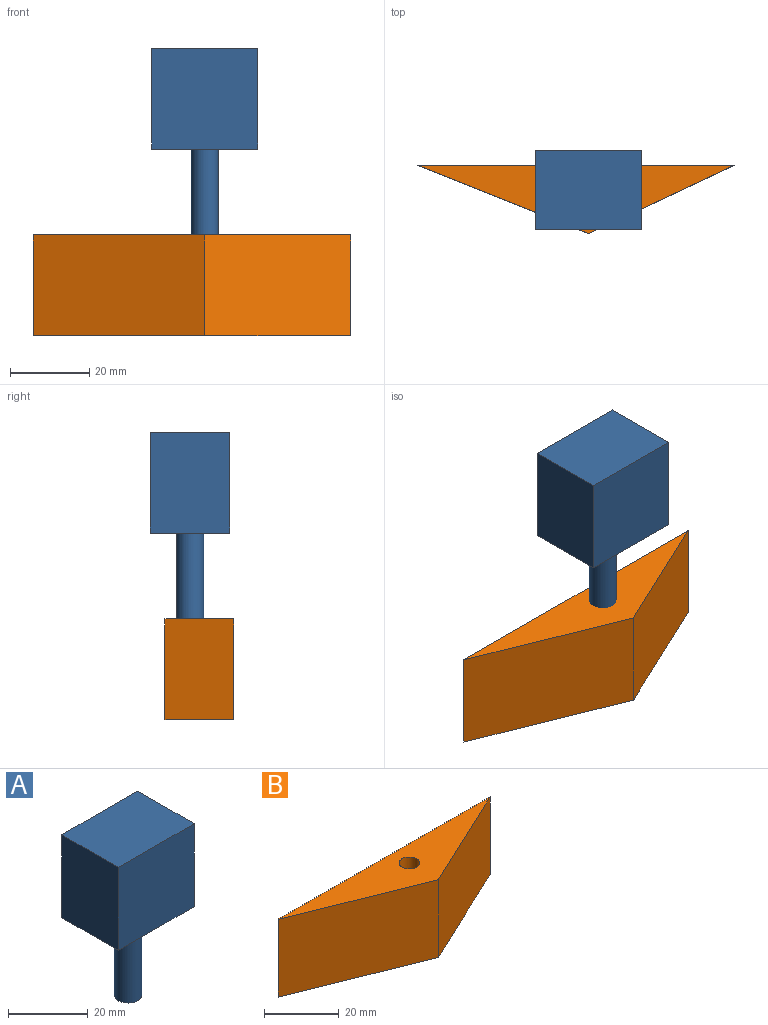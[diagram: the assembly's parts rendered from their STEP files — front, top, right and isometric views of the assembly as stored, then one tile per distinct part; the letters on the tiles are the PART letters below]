
ASSEMBLY  parts=2 mates=1
PART A: 8 faces, bbox 26.8x20x50.8 mm
  f0: cylinder r=3.43mm len=25.4mm, axis (0,0,-1), area 547.2mm2, adj f1,f7
  f1: plane 6.86x6.86mm, normal (0,0,-1), area 36.9mm2, adj f0
  f2: plane 26.8x25.4mm, normal (0,-1,0), area 680.7mm2, adj f3,f5,f6,f7
  f3: plane 25.4x20.02mm, normal (1,0,0), area 508.5mm2, adj f2,f4,f6,f7
  f4: plane 26.8x25.4mm, normal (0,1,0), area 680.7mm2, adj f3,f5,f6,f7
  f5: plane 25.4x20.02mm, normal (-1,0,0), area 508.5mm2, adj f2,f4,f6,f7
  f6: plane 26.8x20.02mm, normal (0,0,1), area 536.5mm2, adj f2,f3,f4,f5
  f7: plane 26.8x20.02mm, normal (0,0,-1), area 499.6mm2, adj f0,f2,f3,f4,f5
PART B: 6 faces, bbox 80x17.3x25.4 mm
  f0: plane 36.8x25.4mm, normal (0.43,-0.91,0), area 1032.8mm2, adj f1,f2,f3,f4
  f1: plane 80.02x25.4mm, normal (0,1,0), area 2032.5mm2, adj f0,f2,f3,f4
  f2: plane 43.22x25.4mm, normal (-0.37,-0.93,0), area 1182.3mm2, adj f0,f1,f3,f4
  f3: plane 80.02x17.29mm, normal (0,0,1), area 668mm2, adj f0,f1,f2,f5
  f4: plane 80.02x17.29mm, normal (0,0,-1), area 668mm2, adj f0,f1,f2,f5
  f5: cylinder r=2.75mm len=25.4mm, axis (0,0,1), area 438.9mm2, adj f3,f4
PLACE A t=(-14.56,15.89,20.82)mm
PLACE B t=(-14.56,4.95,-0.86)mm fixed
MATE slider A.f0 <-> B.f5  axis (0,0,-1) through (-14.56,15.89,33.52)mm
